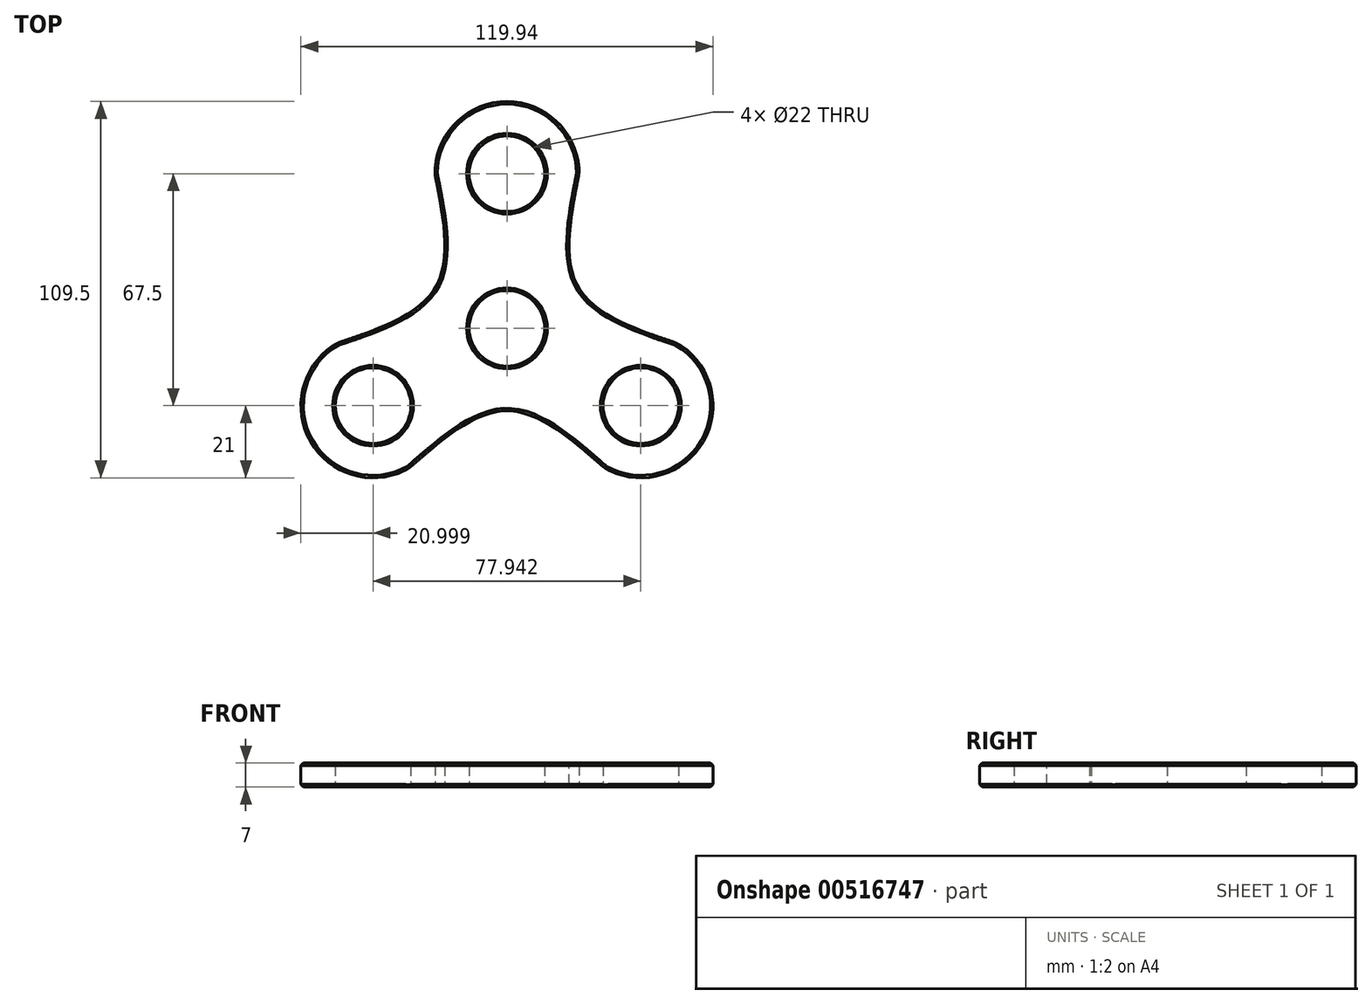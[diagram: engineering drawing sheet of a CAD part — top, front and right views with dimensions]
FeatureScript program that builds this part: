
annotation { "Feature Type Name" : "Feature", "Feature Type Description" : "" }
export const myFeature = defineFeature(function(context is Context, id is Id, definition is map)
    precondition{}
    {
        {
            var Q0;
            Q0=qCreatedBy(makeId("Top.planeOp"),FACE);
            var sketch = newSketch(context, id + "F0", { "sketchPlane" : qUnion([Q0])});
            skSolve(sketch);
        }
        {
            var Q0;
            Q0=qCreatedBy(makeId("Top.planeOp"),FACE);
            var sketch = newSketch(context, id + "F1", { "sketchPlane" : qUnion([Q0])});
            skCircle(sketch, "E0", {"center": v(0, 0) * mm, "radius": 11 * mm});
            skLineSegment(sketch, "E1", {"start": v(0, 0) * mm, "end": v(0, 45) * mm, "construction": true});
            skLineSegment(sketch, "E2", {"start": v(0, 0) * mm, "end": v(38.97, -22.5) * mm, "construction": true});
            skLineSegment(sketch, "E3", {"start": v(0, 0) * mm, "end": v(-38.97, -22.5) * mm, "construction": true});
            skCircle(sketch, "E4", {"center": v(38.97, -22.5) * mm, "radius": 11 * mm});
            skCircle(sketch, "E5", {"center": v(0, 45) * mm, "radius": 11 * mm});
            skCircle(sketch, "E6", {"center": v(-38.97, -22.5) * mm, "radius": 11 * mm});
            skCircle(sketch, "E7", {"center": v(0, 0) * mm, "radius": 20 * mm});
            skArc(sketch, "E8", {"start": v(19.5, 37.2) * mm, "mid": v(0, 66) * mm, "end": v(-19.5, 37.2) * mm});
            skArc(sketch, "E9", {"start": v(22.47, -35.49) * mm, "mid": v(57.16, -33) * mm, "end": v(41.97, -1.72) * mm});
            skArc(sketch, "E10", {"start": v(-41.97, -1.72) * mm, "mid": v(-57.16, -33) * mm, "end": v(-22.47, -35.49) * mm});
            skLineSegment(sketch, "E11", {"start": v(38.97, -22.5) * mm, "end": v(-38.97, 22.5) * mm, "construction": true});
            skLineSegment(sketch, "E12", {"start": v(-38.97, -22.5) * mm, "end": v(38.97, 22.5) * mm, "construction": true});
            skLineSegment(sketch, "E13", {"start": v(0, 0) * mm, "end": v(0, -45) * mm, "construction": true});
            skPoint(sketch, "E14", {"position": v(-21, 45) * mm});
            skPoint(sketch, "E15", {"position": v(-49.47, -4.31) * mm});
            skPoint(sketch, "E16", {"position": v(-28.47, -40.69) * mm});
            skPoint(sketch, "E17", {"position": v(49.47, -4.31) * mm});
            skPoint(sketch, "E18", {"position": v(28.47, -40.69) * mm});
            skPoint(sketch, "E19", {"position": v(-20.78, 12) * mm});
            skPoint(sketch, "E20", {"position": v(20.78, 12) * mm});
            skPoint(sketch, "E21", {"position": v(0, -24) * mm});
            skFitSpline(sketch, "E22", {"points": [v(-21, 45) * mm, v(-20.78, 12) * mm, v(-49.47, -4.31) * mm], "startDerivative": vector(14.88, -74.34) * mm, "endDerivative": vector(-71.82, -24.28) * mm});
            skFitSpline(sketch, "E23", {"points": [v(21, 45) * mm, v(20.78, 12) * mm, v(49.47, -4.31) * mm], "startDerivative": vector(-14.88, -74.34) * mm, "endDerivative": vector(71.82, -24.28) * mm});
            skFitSpline(sketch, "E24", {"points": [v(28.47, -40.69) * mm, v(0, -24) * mm, v(-28.47, -40.69) * mm], "startDerivative": vector(-56.94, 50.06) * mm, "endDerivative": vector(-56.94, -50.06) * mm});
            skPoint(sketch, "E25", {"position": v(-57.16, -33) * mm});
            skPoint(sketch, "E26", {"position": v(0, 66) * mm});
            skSolve(sketch);
        }
        {
            var Q0;
            Q0 = qSketchRegion(id + "F0", true);
            var Q1;
            Q1=makeQuery(id+"F1.imprint","IMPRINT",FACE,{"disambiguationData":[TD([[makeQuery(id+"F1.imprint","IMPRINT",EDGE,{"derivedFrom":sQuery(id+"F1.wireOp",EDGE,"E4")}),-1.0]])]});
            var Q2;
            Q2=makeQuery(id+"F1.imprint","IMPRINT",FACE,{"disambiguationData":[TD([[makeQuery(id+"F1.imprint","IMPRINT",EDGE,{"derivedFrom":sQuery(id+"F1.wireOp",EDGE,"E0")}),-1.0]])]});
            extrude(context, id + "F2", {"entities" : qUnion([Q0, Q1, Q2]), "depth" : 7 * mm, "offsetDistance" : 25 * mm});
        }
        {
            var Q0;
            Q0=makeQuery(id+"F2.opExtrude","CAP_FACE",FACE,{"disambiguationData":[OSD([sQuery(id+"F1.wireOp",EDGE,"E0"),sQuery(id+"F1.wireOp",EDGE,"E4"),sQuery(id+"F1.wireOp",EDGE,"E5"),sQuery(id+"F1.wireOp",EDGE,"E6"),sQuery(id+"F1.wireOp",EDGE,"E8"),sQuery(id+"F1.wireOp",EDGE,"E9"),sQuery(id+"F1.wireOp",EDGE,"E10"),sQuery(id+"F1.wireOp",EDGE,"E22"),sQuery(id+"F1.wireOp",EDGE,"E23"),sQuery(id+"F1.wireOp",EDGE,"E24")])],"isStart":false});
            var Q1;
            Q1=makeQuery(id+"F2.opExtrude","CAP_FACE",FACE,{"disambiguationData":[OSD([sQuery(id+"F1.wireOp",EDGE,"E0"),sQuery(id+"F1.wireOp",EDGE,"E4"),sQuery(id+"F1.wireOp",EDGE,"E5"),sQuery(id+"F1.wireOp",EDGE,"E6"),sQuery(id+"F1.wireOp",EDGE,"E8"),sQuery(id+"F1.wireOp",EDGE,"E9"),sQuery(id+"F1.wireOp",EDGE,"E10"),sQuery(id+"F1.wireOp",EDGE,"E22"),sQuery(id+"F1.wireOp",EDGE,"E23"),sQuery(id+"F1.wireOp",EDGE,"E24")])],"isStart":true});
            chamfer(context, id + "F3", {"entities" : qUnion([Q0, Q1]), "width" : 0.75 * mm, "tangentPropagation" : true});
        }
        {
            var Q0;
            Q0=makeQuery(id+"F2.opExtrude","SWEPT_EDGE",EDGE,{"disambiguationData":[OSD([sQuery(id+"F1.wireOp",EDGE,"E9"),sQuery(id+"F1.wireOp",EDGE,"E24")])]});
            var Q1;
            Q1=makeQuery(id+"F2.opExtrude","SWEPT_EDGE",EDGE,{"disambiguationData":[OSD([sQuery(id+"F1.wireOp",EDGE,"E10"),sQuery(id+"F1.wireOp",EDGE,"E24")])]});
            var Q2;
            Q2=makeQuery(id+"F2.opExtrude","SWEPT_EDGE",EDGE,{"disambiguationData":[OSD([sQuery(id+"F1.wireOp",EDGE,"E10"),sQuery(id+"F1.wireOp",EDGE,"E22")])]});
            var Q3;
            Q3=makeQuery(id+"F2.opExtrude","SWEPT_EDGE",EDGE,{"disambiguationData":[OSD([sQuery(id+"F1.wireOp",EDGE,"E8"),sQuery(id+"F1.wireOp",EDGE,"E22")])]});
            var Q4;
            Q4=makeQuery(id+"F2.opExtrude","SWEPT_EDGE",EDGE,{"disambiguationData":[OSD([sQuery(id+"F1.wireOp",EDGE,"E8"),sQuery(id+"F1.wireOp",EDGE,"E23")])]});
            var Q5;
            Q5=makeQuery(id+"F2.opExtrude","SWEPT_EDGE",EDGE,{"disambiguationData":[OSD([sQuery(id+"F1.wireOp",EDGE,"E9"),sQuery(id+"F1.wireOp",EDGE,"E23")])]});
            fillet(context, id + "F4", {"entities" : qUnion([Q0, Q1, Q2, Q3, Q4, Q5]), "radius" : 10 * mm, "tangentPropagation" : true, "allowEdgeOverflow" : false});
        }
    });
